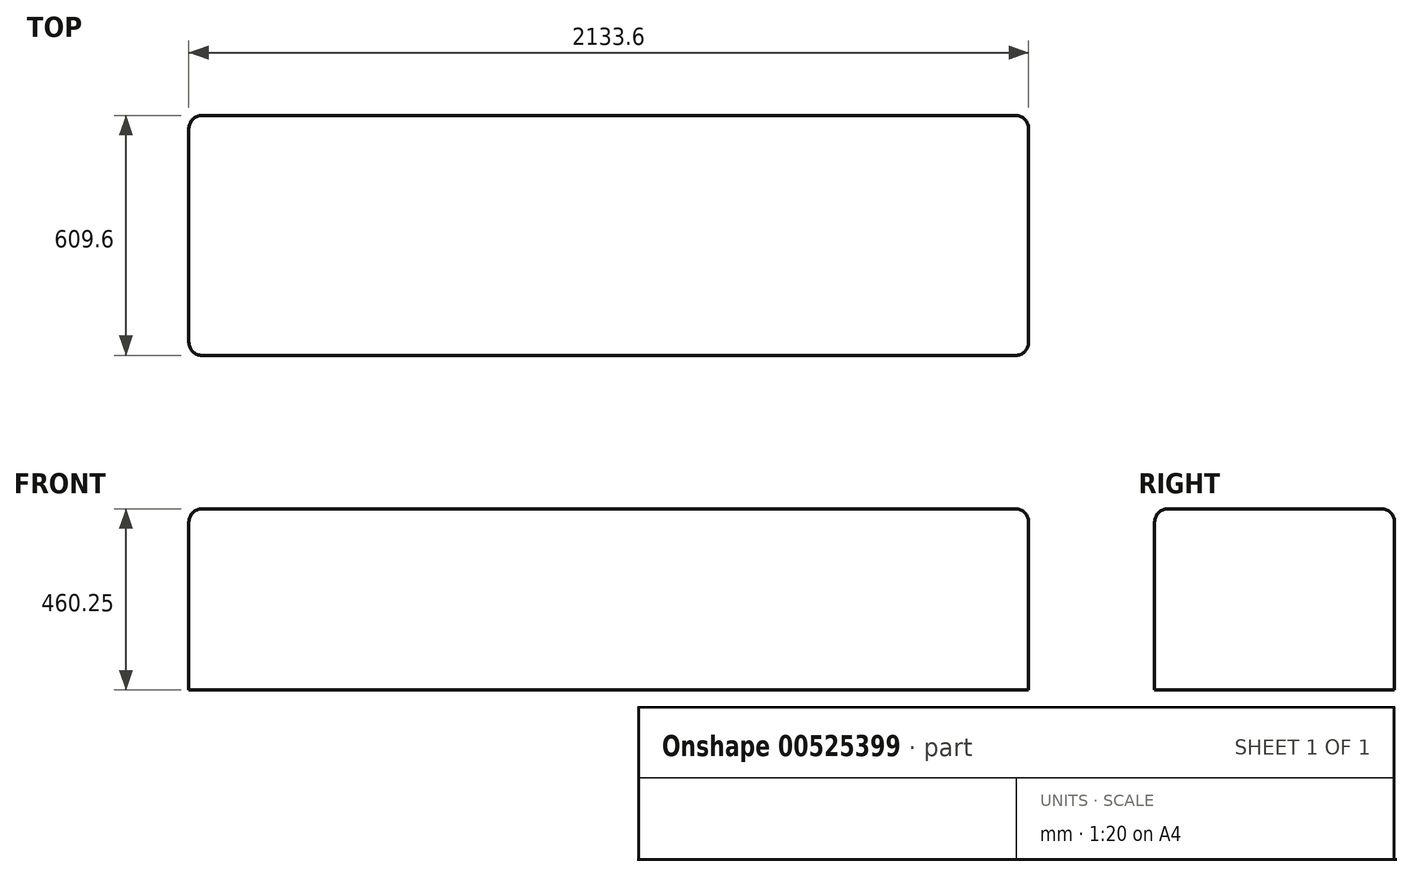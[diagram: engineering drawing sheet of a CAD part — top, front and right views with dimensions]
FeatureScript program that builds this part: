
annotation { "Feature Type Name" : "Feature", "Feature Type Description" : "" }
export const myFeature = defineFeature(function(context is Context, id is Id, definition is map)
    precondition{}
    {
        {
            var Q0;
            Q0=qCreatedBy(makeId("Top.planeOp"),FACE);
            var sketch = newSketch(context, id + "F0", { "sketchPlane" : qUnion([Q0])});
            skLineSegment(sketch, "E0.bottom", {"start": v(1066.8, -304.8) * mm, "end": v(-1066.8, -304.8) * mm});
            skLineSegment(sketch, "E0.top", {"start": v(1066.8, 304.8) * mm, "end": v(-1066.8, 304.8) * mm});
            skLineSegment(sketch, "E0.left", {"start": v(1066.8, -304.8) * mm, "end": v(1066.8, 304.8) * mm});
            skLineSegment(sketch, "E0.right", {"start": v(-1066.8, -304.8) * mm, "end": v(-1066.8, 304.8) * mm});
            skPoint(sketch, "E0.middle", {"position": v(0, 0) * mm});
            skSolve(sketch);
        }
        {
            var Q0;
            Q0=makeQuery(id+"F0.imprint","IMPRINT",FACE,{"disambiguationData":[TD([[makeQuery(id+"F0.imprint","IMPRINT",EDGE,{"derivedFrom":sQuery(id+"F0.wireOp",EDGE,"E0.bottom")}),-1.0]])]});
            extrude(context, id + "F1", {"entities" : qUnion([Q0]), "depth" : 460.25 * mm, "offsetDistance" : 30.48 * mm});
        }
        {
            var Q0;
            Q0=makeQuery(id+"F1.opExtrude","SWEPT_EDGE",EDGE,{"disambiguationData":[OSD([sQuery(id+"F0.wireOp",EDGE,"E0.bottom"),sQuery(id+"F0.wireOp",EDGE,"E0.left")])]});
            var Q1;
            Q1=makeQuery(id+"F1.opExtrude","SWEPT_EDGE",EDGE,{"disambiguationData":[OSD([sQuery(id+"F0.wireOp",EDGE,"E0.top"),sQuery(id+"F0.wireOp",EDGE,"E0.left")])]});
            var Q2;
            Q2=makeQuery(id+"F1.opExtrude","SWEPT_EDGE",EDGE,{"disambiguationData":[OSD([sQuery(id+"F0.wireOp",EDGE,"E0.bottom"),sQuery(id+"F0.wireOp",EDGE,"E0.right")])]});
            var Q3;
            Q3=makeQuery(id+"F1.opExtrude","SWEPT_EDGE",EDGE,{"disambiguationData":[OSD([sQuery(id+"F0.wireOp",EDGE,"E0.top"),sQuery(id+"F0.wireOp",EDGE,"E0.right")])]});
            fillet(context, id + "F2", {"entities" : qUnion([Q0, Q1, Q2, Q3]), "radius" : 33.53 * mm, "tangentPropagation" : true, "allowEdgeOverflow" : false});
        }
        {
            var Q0;
            Q0=makeQuery(id+"F1.opExtrude","CAP_EDGE",EDGE,{"disambiguationData":[OSD([sQuery(id+"F0.wireOp",EDGE,"E0.bottom")])],"isStart":false});
            fillet(context, id + "F3", {"entities" : qUnion([Q0]), "radius" : 33.53 * mm, "tangentPropagation" : true, "allowEdgeOverflow" : false});
        }
    });
